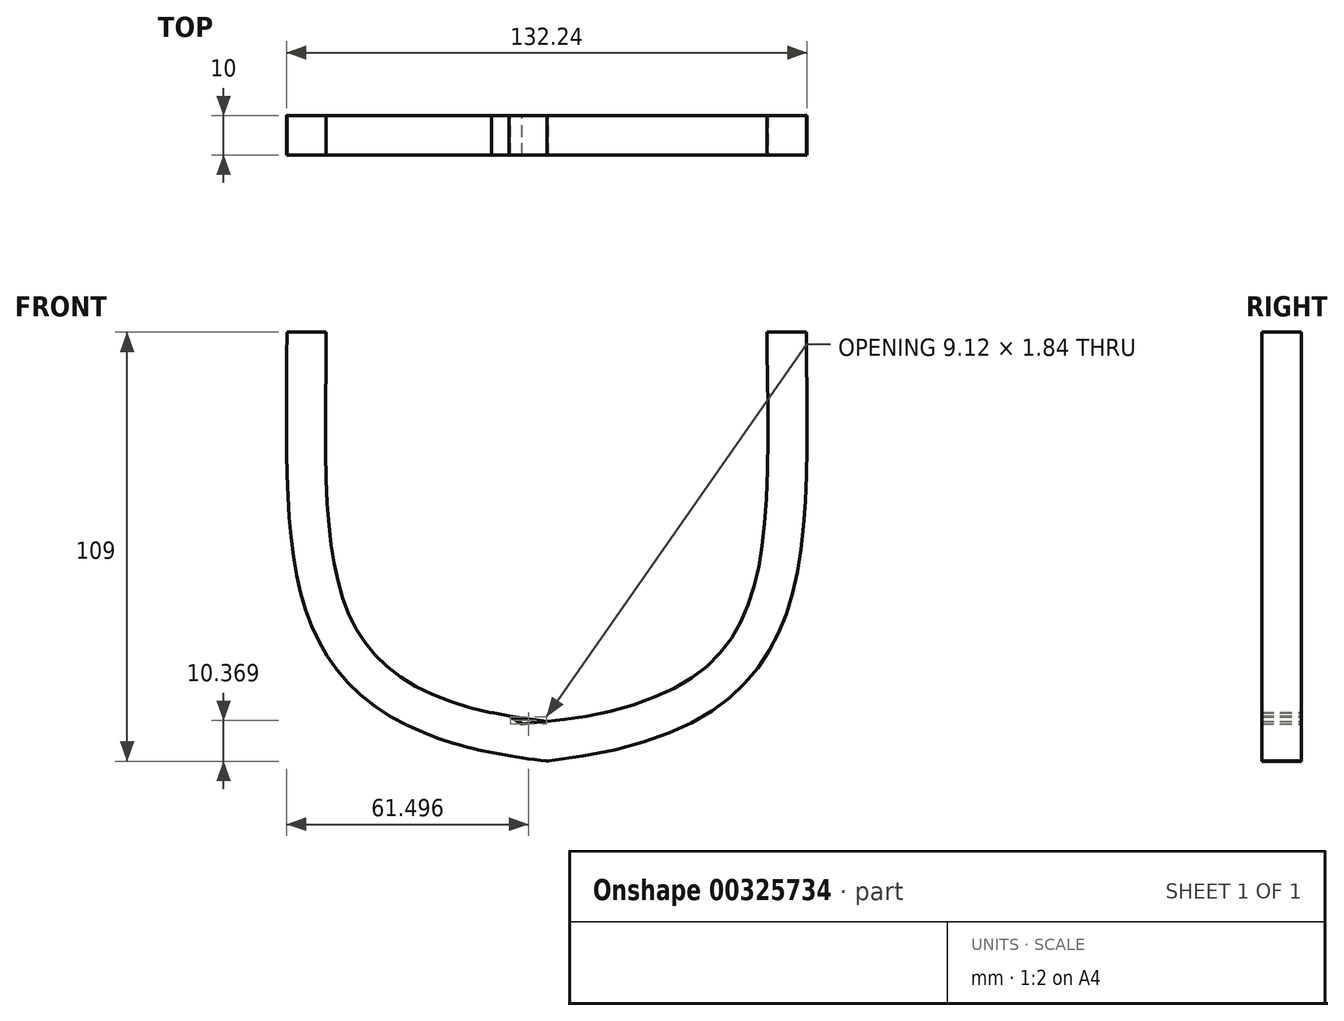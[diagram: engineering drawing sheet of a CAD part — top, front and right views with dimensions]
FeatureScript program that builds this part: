
annotation { "Feature Type Name" : "Feature", "Feature Type Description" : "" }
export const myFeature = defineFeature(function(context is Context, id is Id, definition is map)
    precondition{}
    {
        {
            var Q0;
            Q0=qCreatedBy(makeId("Front.planeOp"),FACE);
            var sketch = newSketch(context, id + "F0", { "sketchPlane" : qUnion([Q0])});
            skPoint(sketch, "E0.endSnap0", {"position": v(-0.41, 0) * mm});
            skLineSegment(sketch, "E1", {"start": v(-65.99, 0) * mm, "end": v(66.01, 0) * mm, "construction": true});
            skLineSegment(sketch, "E2", {"start": v(66.01, 0) * mm, "end": v(66.01, 109) * mm, "construction": true});
            skLineSegment(sketch, "E3", {"start": v(0, 0) * mm, "end": v(0, 142.95) * mm, "construction": true});
            skFitSpline(sketch, "E4", {"points": [v(-0.41, 0) * mm, v(66.01, 109) * mm], "startDerivative": vector(216.3, 23.12) * mm, "endDerivative": vector(0, 181.21) * mm});
            skPoint(sketch, "E5", {"position": v(66.01, 54.5) * mm});
            skFitSpline(sketch, "E6.MirrorCS", {"points": [v(0.41, 0) * mm, v(-66.01, 109) * mm], "startDerivative": vector(-216.3, 23.12) * mm, "endDerivative": vector(0, 181.21) * mm});
            skFitSpline(sketch, "E7.0", {"points": [v(1.48, 9.94) * mm, v(-2.8, 10.4) * mm, v(-10.68, 11.55) * mm, v(-20.63, 13.92) * mm, v(-28.82, 16.86) * mm, v(-35.4, 20.26) * mm, v(-40.62, 24.06) * mm, v(-44.74, 28.26) * mm, v(-48.03, 32.97) * mm, v(-50.67, 38.36) * mm, v(-52.72, 44.54) * mm, v(-54.23, 51.55) * mm, v(-55.25, 59.36) * mm, v(-56.04, 70.78) * mm, v(-56.2, 86.85) * mm, v(-56.01, 101.37) * mm, v(-56.01, 109) * mm]});
            skFitSpline(sketch, "E8.0", {"points": [v(-1.48, 9.94) * mm, v(2.8, 10.4) * mm, v(10.68, 11.55) * mm, v(20.63, 13.92) * mm, v(28.82, 16.86) * mm, v(35.4, 20.26) * mm, v(40.62, 24.06) * mm, v(44.74, 28.26) * mm, v(48.03, 32.97) * mm, v(50.67, 38.36) * mm, v(52.72, 44.54) * mm, v(54.23, 51.55) * mm, v(55.25, 59.36) * mm, v(56.04, 70.78) * mm, v(56.2, 86.85) * mm, v(56.01, 101.37) * mm, v(56.01, 109) * mm]});
            skLineSegment(sketch, "E9", {"start": v(56.01, 109) * mm, "end": v(66.01, 109) * mm});
            skLineSegment(sketch, "E10", {"start": v(-66.01, 109) * mm, "end": v(-56.01, 109) * mm});
            skLineSegment(sketch, "E11", {"start": v(-65.99, 0) * mm, "end": v(-65.99, 143.14) * mm, "construction": true});
            skLineSegment(sketch, "E12", {"start": v(0.02, 10.1) * mm, "end": v(0.41, 0) * mm});
            skLineSegment(sketch, "E13", {"start": v(0.02, 10.1) * mm, "end": v(-30.46, 6.9) * mm});
            skLineSegment(sketch, "E14", {"start": v(-30.46, 6.9) * mm, "end": v(-42.95, 26.5) * mm, "construction": true});
            skLineSegment(sketch, "E15", {"start": v(-42.95, 26.5) * mm, "end": v(-25.36, 7.44) * mm, "construction": true});
            skLineSegment(sketch, "E16", {"start": v(-25.36, 7.44) * mm, "end": v(-23.74, 15.1) * mm, "construction": true});
            skLineSegment(sketch, "E17", {"start": v(-23.74, 15.1) * mm, "end": v(-15.22, 8.5) * mm, "construction": true});
            skLineSegment(sketch, "E18", {"start": v(-15.22, 8.5) * mm, "end": v(-13.98, 10.1) * mm});
            skLineSegment(sketch, "E19", {"start": v(-13.98, 10.1) * mm, "end": v(-13.98, 12.4) * mm});
            skLineSegment(sketch, "E20", {"start": v(-13.98, 12.4) * mm, "end": v(-9.52, 11.5) * mm});
            skLineSegment(sketch, "E21", {"start": v(-9.52, 11.5) * mm, "end": v(-6.26, 9.45) * mm});
            skLineSegment(sketch, "E22", {"start": v(0.02, 10.1) * mm, "end": v(-9.52, 11.5) * mm});
            skPoint(sketch, "E23", {"position": v(-56.02, 106.13) * mm});
            skPoint(sketch, "E24", {"position": v(56.02, 106.13) * mm});
            skPoint(sketch, "E25", {"position": v(-56.07, 96.13) * mm});
            skPoint(sketch, "E26", {"position": v(56.07, 96.13) * mm});
            skPoint(sketch, "E27", {"position": v(-56.11, 82.63) * mm});
            skPoint(sketch, "E28", {"position": v(56.11, 82.63) * mm});
            skPoint(sketch, "E29", {"position": v(-37.86, 96.25) * mm});
            skPoint(sketch, "E30", {"position": v(37.86, 96.13) * mm});
            skLineSegment(sketch, "E31", {"start": v(-56.07, 96.13) * mm, "end": v(-37.86, 96.25) * mm});
            skLineSegment(sketch, "E32", {"start": v(-56.11, 82.63) * mm, "end": v(-37.86, 96.25) * mm});
            skLineSegment(sketch, "E33", {"start": v(37.86, 96.13) * mm, "end": v(56.07, 96.13) * mm});
            skLineSegment(sketch, "E34", {"start": v(56.11, 82.63) * mm, "end": v(37.86, 96.13) * mm});
            skSolve(sketch);
        }
        {
            var Q0;
            Q0 = qSketchRegion(id + "F0", true);
            extrude(context, id + "F1", {"entities" : qUnion([Q0]), "depth" : 10 * mm});
        }
    });
